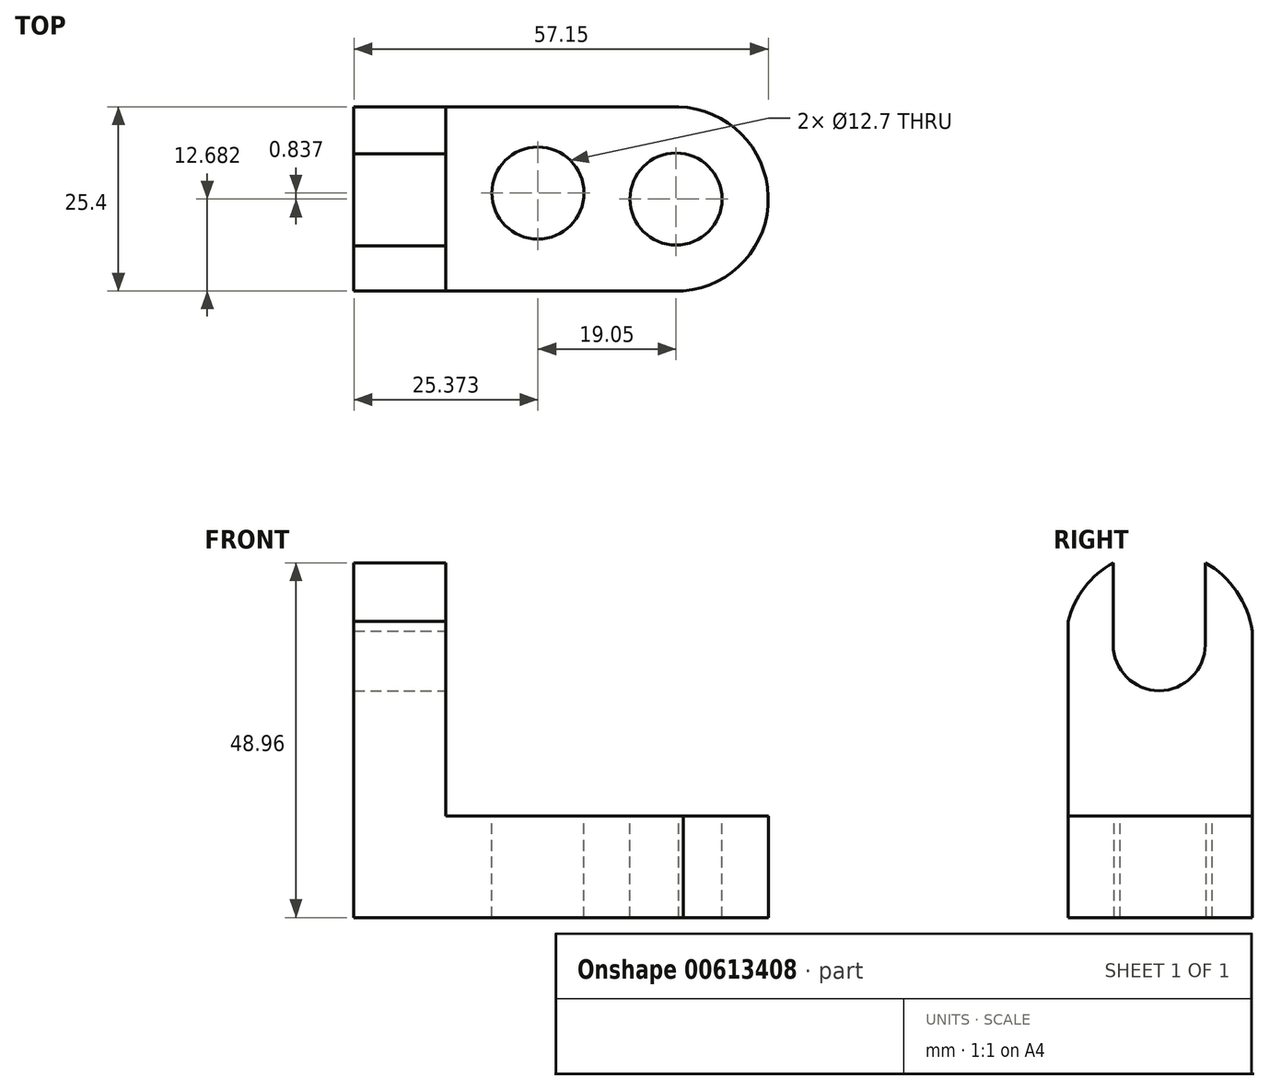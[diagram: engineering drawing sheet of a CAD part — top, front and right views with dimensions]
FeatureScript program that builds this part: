
annotation { "Feature Type Name" : "Feature", "Feature Type Description" : "" }
export const myFeature = defineFeature(function(context is Context, id is Id, definition is map)
    precondition{}
    {
        {
            var Q0;
            Q0=qCreatedBy(makeId("Front.planeOp"),FACE);
            var sketch = newSketch(context, id + "F0", { "sketchPlane" : qUnion([Q0])});
            skLineSegment(sketch, "E0", {"start": v(-53.91, 66.43) * mm, "end": v(-53.91, 15.63) * mm});
            skLineSegment(sketch, "E1", {"start": v(-53.91, 15.63) * mm, "end": v(3.24, 15.63) * mm});
            skLineSegment(sketch, "E2", {"start": v(3.24, 15.63) * mm, "end": v(3.24, 29.64) * mm});
            skLineSegment(sketch, "E3", {"start": v(3.24, 29.64) * mm, "end": v(-41.21, 29.64) * mm});
            skLineSegment(sketch, "E4", {"start": v(-41.21, 29.64) * mm, "end": v(-41.21, 66.43) * mm});
            skLineSegment(sketch, "E5", {"start": v(-41.21, 66.43) * mm, "end": v(-53.91, 66.43) * mm});
            skSolve(sketch);
        }
        {
            var Q0;
            Q0=makeQuery(id+"F0.imprint","IMPRINT",FACE,{"disambiguationData":[TD([[makeQuery(id+"F0.imprint","IMPRINT",EDGE,{"derivedFrom":sQuery(id+"F0.wireOp",EDGE,"E0")}),1.0]])]});
            extrude(context, id + "F1", {"entities" : qUnion([Q0]), "depth" : 25.4 * mm, "offsetDistance" : 25.4 * mm});
        }
        {
            var Q0;
            Q0=makeQuery(id+"F1.opExtrude","SWEPT_FACE",FACE,{"disambiguationData":[OSD([sQuery(id+"F0.wireOp",EDGE,"E4")])]});
            var sketch = newSketch(context, id + "F2", { "sketchPlane" : qUnion([Q0])});
            skArc(sketch, "E6", {"start": v(0, 55.14) * mm, "mid": v(-12.14, 66.24) * mm, "end": v(-25.4, 56.5) * mm});
            skSolve(sketch);
        }
        {
            var Q0;
            {var subQ0=sQuery(id+"F2.wireOp",EDGE,"E6");Q0=makeQuery(id+"F2.imprint","IMPRINT",FACE,{"disambiguationData":[TD([[makeQuery(id+"F2.imprint","IMPRINT",EDGE,{"derivedFrom":subQ0}),-1.0]])]});}
            extrude(context, id + "F3", {"entities" : qUnion([Q0]), "operationType" : NewBodyOperationType.REMOVE, "endBound" : BoundingType.THROUGH_ALL, "oppositeDirection" : true, "depth" : 25.4 * mm, "offsetDistance" : 25.4 * mm});
        }
        {
            var Q0;
            Q0=makeQuery(id+"F1.opExtrude","SWEPT_FACE",FACE,{"disambiguationData":[OSD([sQuery(id+"F0.wireOp",EDGE,"E3")])]});
            var sketch = newSketch(context, id + "F4", { "sketchPlane" : qUnion([Q0])});
            skArc(sketch, "E7", {"start": v(-8.46, -25.4) * mm, "mid": v(3.23, -12.38) * mm, "end": v(-9.15, 0) * mm});
            skSolve(sketch);
        }
        {
            var Q0;
            {var subQ0=sQuery(id+"F4.wireOp",EDGE,"E7");var subQ1=sQuery(id+"F0.wireOp",EDGE,"E3");var subQ2=makeQuery(id+"F1.opExtrude","CAP_EDGE",EDGE,{"disambiguationData":[OSD([subQ1])],"isStart":true});var subQ3=makeQuery(id+"F4.imprint","INTERSECT",VERTEX,{"derivedFrom":[subQ2,subQ0]});Q0=makeQuery(id+"F4.imprint","IMPRINT",FACE,{"disambiguationData":[TD([[makeQuery(id+"F4.imprint","IMPRINT",EDGE,{"disambiguationData":[TD([[subQ3,1.0]])],"derivedFrom":subQ0}),-1.0]])]});}
            var Q1;
            {var subQ0=sQuery(id+"F4.wireOp",EDGE,"E7");var subQ1=sQuery(id+"F0.wireOp",EDGE,"E3");var subQ2=makeQuery(id+"F1.opExtrude","CAP_EDGE",EDGE,{"disambiguationData":[OSD([subQ1])],"isStart":false});var subQ3=makeQuery(id+"F4.imprint","INTERSECT",VERTEX,{"derivedFrom":[subQ2,subQ0]});Q1=makeQuery(id+"F4.imprint","IMPRINT",FACE,{"disambiguationData":[TD([[makeQuery(id+"F4.imprint","IMPRINT",EDGE,{"disambiguationData":[TD([[subQ3,-1.0]])],"derivedFrom":subQ0}),-1.0]])]});}
            extrude(context, id + "F5", {"entities" : qUnion([Q0, Q1]), "operationType" : NewBodyOperationType.REMOVE, "endBound" : BoundingType.THROUGH_ALL, "oppositeDirection" : true, "depth" : 25.4 * mm, "offsetDistance" : 25.4 * mm});
        }
        {
            var Q0;
            Q0=makeQuery(id+"F1.opExtrude","SWEPT_FACE",FACE,{"disambiguationData":[OSD([sQuery(id+"F0.wireOp",EDGE,"E3")])]});
            var sketch = newSketch(context, id + "F6", { "sketchPlane" : qUnion([Q0])});
            skCircle(sketch, "E8", {"center": v(-28.54, -11.88) * mm, "radius": 6.35 * mm});
            skCircle(sketch, "E9", {"center": v(-9.49, -12.72) * mm, "radius": 6.35 * mm});
            skSolve(sketch);
        }
        {
            var Q0;
            Q0=makeQuery(id+"F6.imprint","IMPRINT",FACE,{"disambiguationData":[TD([[makeQuery(id+"F6.imprint","IMPRINT",EDGE,{"derivedFrom":sQuery(id+"F6.wireOp",EDGE,"E8")}),1.0]])]});
            var Q1;
            Q1=makeQuery(id+"F6.imprint","IMPRINT",FACE,{"disambiguationData":[TD([[makeQuery(id+"F6.imprint","IMPRINT",EDGE,{"derivedFrom":sQuery(id+"F6.wireOp",EDGE,"E9")}),1.0]])]});
            extrude(context, id + "F7", {"entities" : qUnion([Q0, Q1]), "operationType" : NewBodyOperationType.REMOVE, "endBound" : BoundingType.THROUGH_ALL, "oppositeDirection" : true, "depth" : 25.4 * mm, "offsetDistance" : 25.4 * mm});
        }
        {
            var Q0;
            Q0=makeQuery(id+"F1.opExtrude","SWEPT_FACE",FACE,{"disambiguationData":[OSD([sQuery(id+"F0.wireOp",EDGE,"E4")])]});
            var sketch = newSketch(context, id + "F8", { "sketchPlane" : qUnion([Q0])});
            skCircle(sketch, "E10", {"center": v(-12.84, 53.29) * mm, "radius": 6.35 * mm});
            skLineSegment(sketch, "E11", {"start": v(-19.19, 53.29) * mm, "end": v(-19.19, 64.6) * mm});
            skLineSegment(sketch, "E12", {"start": v(-6.49, 53.29) * mm, "end": v(-6.49, 64.6) * mm});
            skSolve(sketch);
        }
        {
            var Q0;
            {var subQ0=sQuery(id+"F8.wireOp",EDGE,"E11");Q0=makeQuery(id+"F8.imprint","IMPRINT",FACE,{"disambiguationData":[TD([[makeQuery(id+"F8.imprint","IMPRINT",EDGE,{"derivedFrom":subQ0}),-1.0]])]});}
            var Q1;
            {var subQ0=sQuery(id+"F8.wireOp",EDGE,"E10");var subQ1=makeQuery(id+"F8.imprint","INTERSECT",VERTEX,{"derivedFrom":[subQ0,sQuery(id+"F8.wireOp",EDGE,"E11")]});Q1=makeQuery(id+"F8.imprint","IMPRINT",FACE,{"disambiguationData":[TD([[makeQuery(id+"F8.imprint","IMPRINT",EDGE,{"disambiguationData":[TD([[subQ1,1.0]])],"derivedFrom":subQ0}),1.0]])]});}
            extrude(context, id + "F9", {"entities" : qUnion([Q0, Q1]), "operationType" : NewBodyOperationType.REMOVE, "endBound" : BoundingType.THROUGH_ALL, "oppositeDirection" : true, "depth" : 25.4 * mm, "offsetDistance" : 25.4 * mm});
        }
    });
